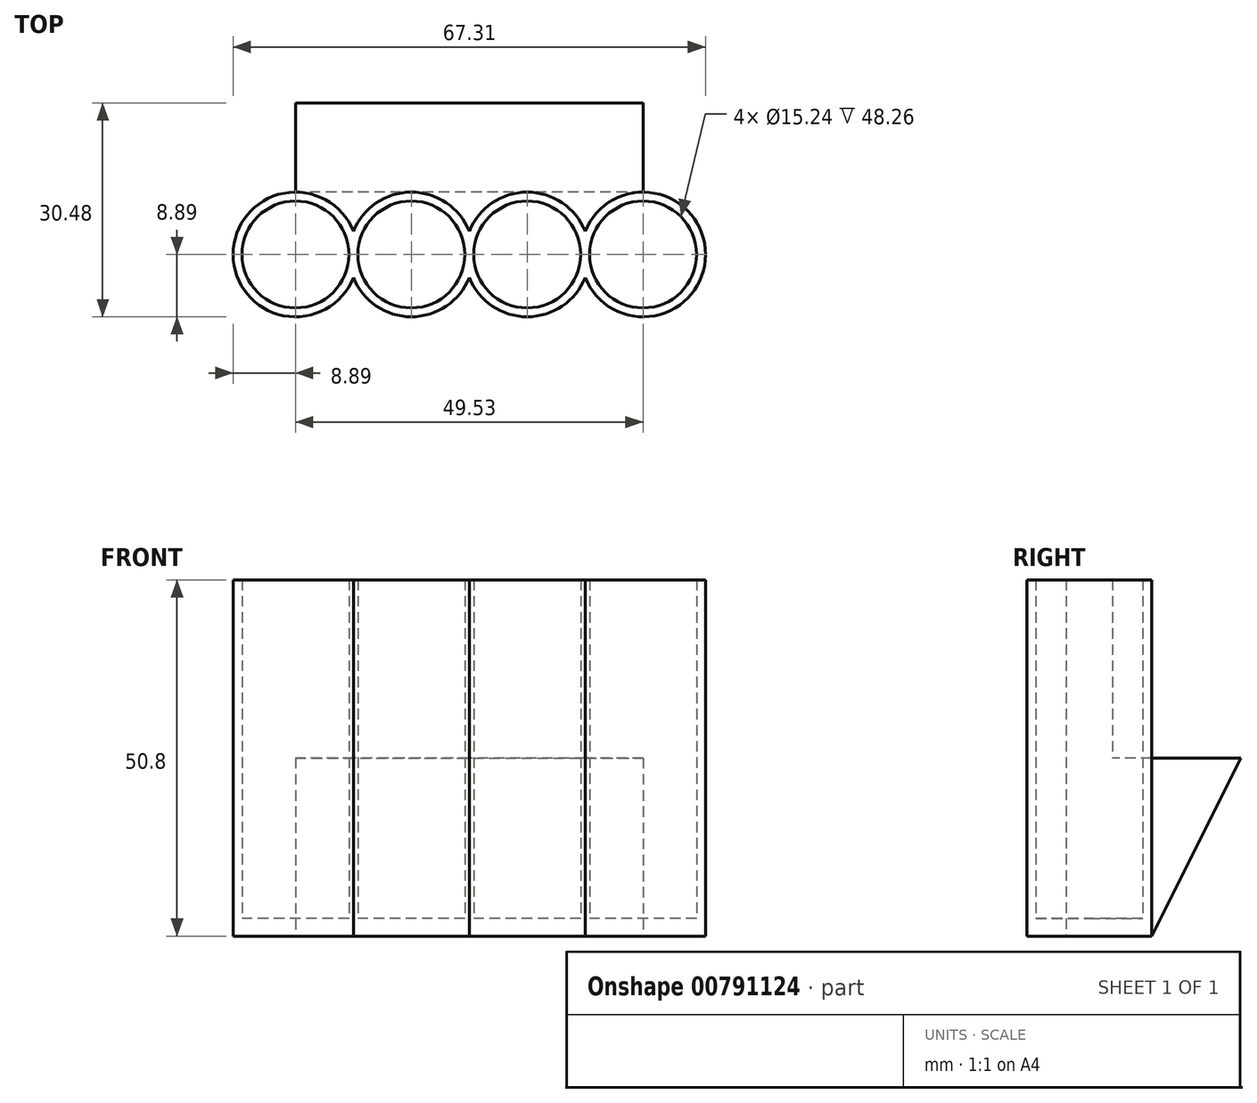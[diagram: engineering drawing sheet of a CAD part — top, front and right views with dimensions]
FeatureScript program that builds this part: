
annotation { "Feature Type Name" : "Feature", "Feature Type Description" : "" }
export const myFeature = defineFeature(function(context is Context, id is Id, definition is map)
    precondition{}
    {
        {
            var Q0;
            Q0=qCreatedBy(makeId("Top.planeOp"),FACE);
            var sketch = newSketch(context, id + "F0", { "sketchPlane" : qUnion([Q0])});
            skCircle(sketch, "E0", {"center": v(0, 0) * mm, "radius": 7.62 * mm});
            skArc(sketch, "E1", {"start": v(8.26, 3.3) * mm, "mid": v(-8.9, 0) * mm, "end": v(8.26, -3.3) * mm});
            skCircle(sketch, "E2", {"center": v(16.51, 0) * mm, "radius": 7.62 * mm});
            skArc(sketch, "E3", {"start": v(8.26, -3.3) * mm, "mid": v(16.51, -8.9) * mm, "end": v(24.77, -3.3) * mm});
            skCircle(sketch, "E4", {"center": v(33.02, 0) * mm, "radius": 7.62 * mm});
            skArc(sketch, "E5", {"start": v(24.77, -3.3) * mm, "mid": v(33.02, -8.89) * mm, "end": v(41.28, -3.3) * mm});
            skCircle(sketch, "E6", {"center": v(49.53, 0) * mm, "radius": 7.62 * mm});
            skArc(sketch, "E7", {"start": v(41.28, -3.3) * mm, "mid": v(58.42, 0) * mm, "end": v(41.28, 3.3) * mm});
            skArc(sketch, "E8.trimOffspring", {"start": v(24.77, 3.3) * mm, "mid": v(16.51, 8.9) * mm, "end": v(8.25, 3.3) * mm});
            skArc(sketch, "E9.trimOffspring", {"start": v(41.28, 3.3) * mm, "mid": v(33.02, 8.9) * mm, "end": v(24.77, 3.3) * mm});
            skLineSegment(sketch, "E10.bottom", {"start": v(0, 8.9) * mm, "end": v(49.53, 8.9) * mm});
            skLineSegment(sketch, "E10.top", {"start": v(0, 21.59) * mm, "end": v(49.53, 21.59) * mm});
            skLineSegment(sketch, "E10.left", {"start": v(0, 8.9) * mm, "end": v(0, 21.59) * mm});
            skLineSegment(sketch, "E10.right", {"start": v(49.53, 8.9) * mm, "end": v(49.53, 21.59) * mm});
            skSolve(sketch);
        }
        {
            var Q0;
            Q0=makeQuery(id+"F0.imprint","IMPRINT",FACE,{"disambiguationData":[TD([[makeQuery(id+"F0.imprint","IMPRINT",EDGE,{"derivedFrom":sQuery(id+"F0.wireOp",EDGE,"E0")}),-1.0]])]});
            extrude(context, id + "F1", {"entities" : qUnion([Q0]), "depth" : 50.8 * mm, "offsetDistance" : 25.4 * mm});
        }
        {
            var Q0;
            {var subQ0=sQuery(id+"F0.wireOp",EDGE,"E9.trimOffspring");var subQ1=sQuery(id+"F0.wireOp",EDGE,"E7");var subQ2=makeQuery(id+"F0.imprint","INTERSECT",VERTEX,{"derivedFrom":[subQ1,subQ0]});Q0=makeQuery(id+"F0.imprint","IMPRINT",FACE,{"disambiguationData":[TD([[makeQuery(id+"F0.imprint","IMPRINT",EDGE,{"disambiguationData":[TD([[subQ2,-1.0]])],"derivedFrom":subQ0}),-1.0]])]});}
            var Q1;
            {var subQ0=sQuery(id+"F0.wireOp",EDGE,"E9.trimOffspring");var subQ1=sQuery(id+"F0.wireOp",EDGE,"E8.trimOffspring");var subQ2=makeQuery(id+"F0.imprint","INTERSECT",VERTEX,{"derivedFrom":[subQ1,subQ0]});Q1=makeQuery(id+"F0.imprint","IMPRINT",FACE,{"disambiguationData":[TD([[makeQuery(id+"F0.imprint","IMPRINT",EDGE,{"disambiguationData":[TD([[subQ2,-1.0]])],"derivedFrom":subQ1}),-1.0]])]});}
            var Q2;
            {var subQ0=sQuery(id+"F0.wireOp",EDGE,"E8.trimOffspring");var subQ1=sQuery(id+"F0.wireOp",EDGE,"E1");var subQ2=makeQuery(id+"F0.imprint","INTERSECT",VERTEX,{"derivedFrom":[subQ1,subQ0]});Q2=makeQuery(id+"F0.imprint","IMPRINT",FACE,{"disambiguationData":[TD([[makeQuery(id+"F0.imprint","IMPRINT",EDGE,{"disambiguationData":[TD([[subQ2,1.0]])],"derivedFrom":subQ0}),-1.0]])]});}
            var Q3;
            Q3=makeQuery(id+"F0.imprint","IMPRINT",FACE,{"disambiguationData":[TD([[makeQuery(id+"F0.imprint","IMPRINT",EDGE,{"derivedFrom":sQuery(id+"F0.wireOp",EDGE,"E10.top")}),-1.0]])]});
            extrude(context, id + "F2", {"entities" : qUnion([Q0, Q1, Q2, Q3]), "operationType" : NewBodyOperationType.ADD, "depth" : 25.4 * mm, "offsetDistance" : 25.4 * mm});
        }
        {
            var Q0;
            Q0=makeQuery(id+"F2.opExtrude","SWEPT_FACE",FACE,{"disambiguationData":[OSD([sQuery(id+"F0.wireOp",EDGE,"E10.left")])]});
            var sketch = newSketch(context, id + "F3", { "sketchPlane" : qUnion([Q0])});
            skLineSegment(sketch, "E11", {"start": v(-21.6, 25.4) * mm, "end": v(-8.89, 0) * mm});
            skLineSegment(sketch, "E12", {"start": v(-8.89, 0) * mm, "end": v(-21.59, 0) * mm});
            skLineSegment(sketch, "E13", {"start": v(-21.59, 0) * mm, "end": v(-21.59, 25.4) * mm});
            skSolve(sketch);
        }
        {
            var Q0;
            Q0=makeQuery(id+"F3.imprint","IMPRINT",FACE,{"disambiguationData":[TD([[makeQuery(id+"F3.imprint","IMPRINT",EDGE,{"derivedFrom":sQuery(id+"F3.wireOp",EDGE,"E11")}),-1.0]])]});
            extrude(context, id + "F4", {"entities" : qUnion([Q0]), "operationType" : NewBodyOperationType.REMOVE, "oppositeDirection" : true, "depth" : 61.47 * mm, "offsetDistance" : 25.4 * mm});
        }
        {
            var Q0;
            Q0=makeQuery(id+"F0.imprint","IMPRINT",FACE,{"disambiguationData":[TD([[makeQuery(id+"F0.imprint","IMPRINT",EDGE,{"derivedFrom":sQuery(id+"F0.wireOp",EDGE,"E0")}),1.0]])]});
            var Q1;
            Q1=makeQuery(id+"F0.imprint","IMPRINT",FACE,{"disambiguationData":[TD([[makeQuery(id+"F0.imprint","IMPRINT",EDGE,{"derivedFrom":sQuery(id+"F0.wireOp",EDGE,"E2")}),1.0]])]});
            var Q2;
            Q2=makeQuery(id+"F0.imprint","IMPRINT",FACE,{"disambiguationData":[TD([[makeQuery(id+"F0.imprint","IMPRINT",EDGE,{"derivedFrom":sQuery(id+"F0.wireOp",EDGE,"E4")}),1.0]])]});
            var Q3;
            Q3=makeQuery(id+"F0.imprint","IMPRINT",FACE,{"disambiguationData":[TD([[makeQuery(id+"F0.imprint","IMPRINT",EDGE,{"derivedFrom":sQuery(id+"F0.wireOp",EDGE,"E6")}),1.0]])]});
            extrude(context, id + "F5", {"entities" : qUnion([Q0, Q1, Q2, Q3]), "operationType" : NewBodyOperationType.ADD, "depth" : 2.54 * mm, "offsetDistance" : 25.4 * mm});
        }
    });
